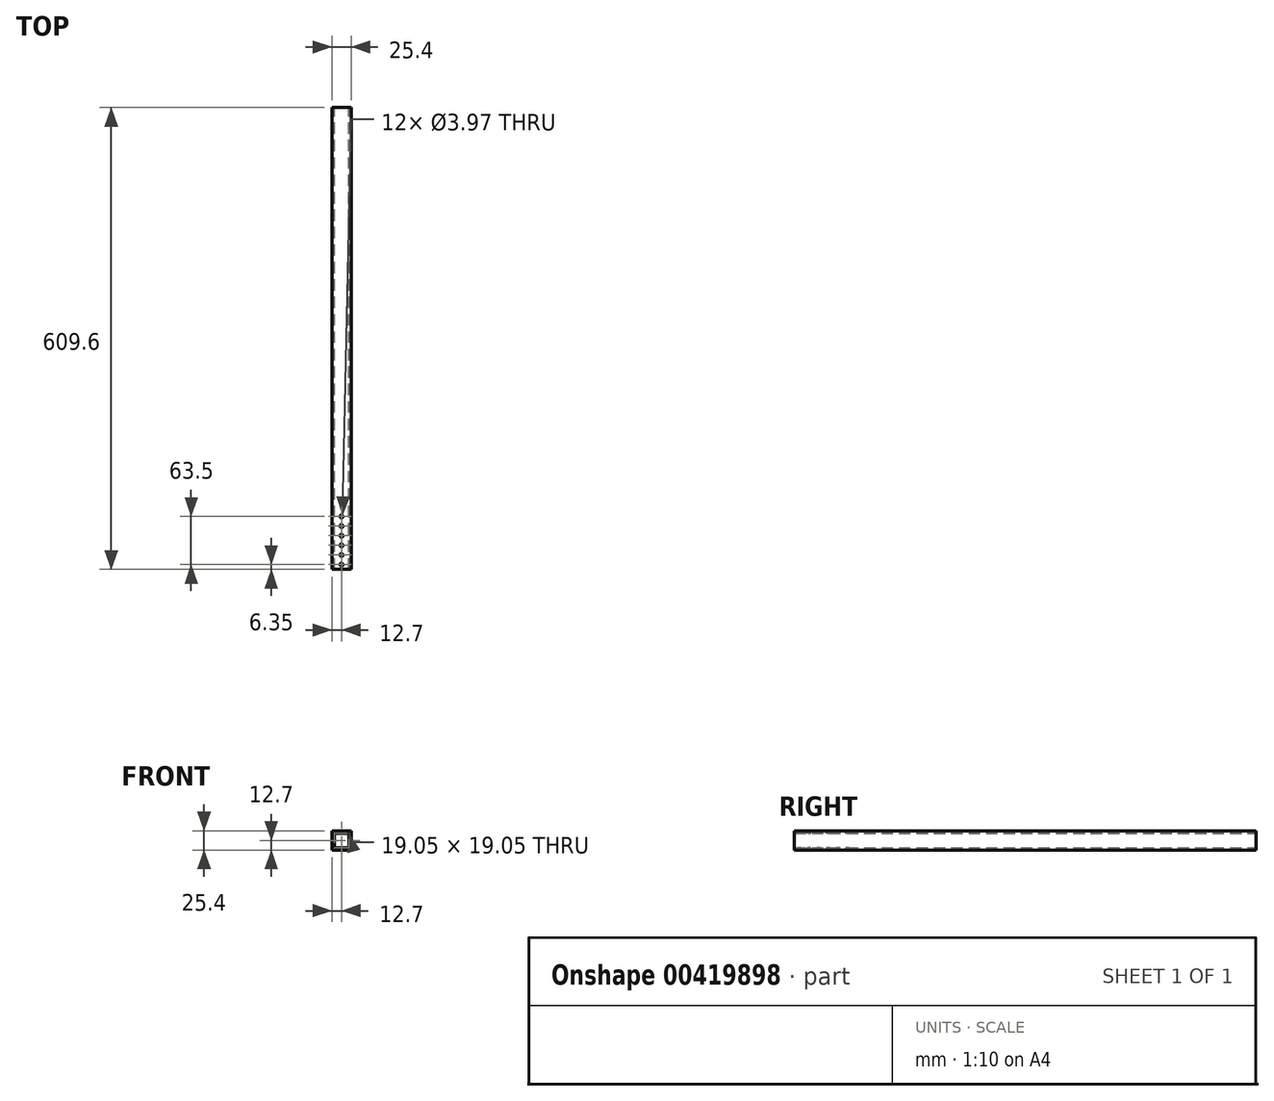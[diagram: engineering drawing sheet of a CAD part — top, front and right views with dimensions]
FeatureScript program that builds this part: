
annotation { "Feature Type Name" : "Feature", "Feature Type Description" : "" }
export const myFeature = defineFeature(function(context is Context, id is Id, definition is map)
    precondition{}
    {
        {
            var Q0;
            Q0=qCreatedBy(makeId("Front.planeOp"),FACE);
            var sketch = newSketch(context, id + "F0", { "sketchPlane" : qUnion([Q0])});
            skPoint(sketch, "E0.middle", {"position": v(0, 0) * mm});
            skLineSegment(sketch, "E1.bottom", {"start": v(12.7, 12.7) * mm, "end": v(-12.7, 12.7) * mm});
            skLineSegment(sketch, "E1.top", {"start": v(12.7, -12.7) * mm, "end": v(-12.7, -12.7) * mm});
            skLineSegment(sketch, "E1.left", {"start": v(12.7, 12.7) * mm, "end": v(12.7, -12.7) * mm});
            skLineSegment(sketch, "E1.right", {"start": v(-12.7, 12.7) * mm, "end": v(-12.7, -12.7) * mm});
            skLineSegment(sketch, "E2.bottom", {"start": v(9.52, 9.53) * mm, "end": v(-9.53, 9.53) * mm});
            skLineSegment(sketch, "E2.top", {"start": v(9.53, -9.53) * mm, "end": v(-9.52, -9.53) * mm});
            skLineSegment(sketch, "E2.left", {"start": v(9.52, 9.53) * mm, "end": v(9.53, -9.53) * mm});
            skLineSegment(sketch, "E2.right", {"start": v(-9.53, 9.53) * mm, "end": v(-9.52, -9.53) * mm});
            skSolve(sketch);
        }
        {
            var Q0;
            Q0 = qSketchRegion(id + "F0", true);
            extrude(context, id + "F1", {"entities" : qUnion([Q0]), "endBound" : BoundingType.SYMMETRIC, "depth" : 609.6 * mm});
        }
        {
            var Q0;
            Q0=makeQuery(id+"F1.opExtrude","SWEPT_FACE",FACE,{"disambiguationData":[OSD([sQuery(id+"F0.wireOp",EDGE,"E1.bottom")])]});
            var sketch = newSketch(context, id + "F2", { "sketchPlane" : qUnion([Q0])});
            skCircle(sketch, "E3", {"center": v(0, -298.45) * mm, "radius": 1.98 * mm});
            skCircle(sketch, "E4", {"center": v(0, -112.92) * mm, "radius": 1.36 * mm});
            skCircle(sketch, "E5", {"center": v(0, -107.45) * mm, "radius": 1.5 * mm});
            skCircle(sketch, "E6", {"center": v(0, -285.75) * mm, "radius": 1.98 * mm});
            skCircle(sketch, "E7.0.1.0", {"center": v(0, -273.05) * mm, "radius": 1.98 * mm});
            skCircle(sketch, "E7.0.2.0", {"center": v(0, -260.35) * mm, "radius": 1.98 * mm});
            skCircle(sketch, "E7.0.3.0", {"center": v(0, -247.65) * mm, "radius": 1.98 * mm});
            skCircle(sketch, "E7.0.4.0", {"center": v(0, -234.95) * mm, "radius": 1.98 * mm});
            skCircle(sketch, "E7.0.5.0", {"center": v(0, -222.25) * mm, "radius": 1.98 * mm});
            skCircle(sketch, "E7.0.6.0", {"center": v(0, -209.55) * mm, "radius": 1.98 * mm});
            skCircle(sketch, "E7.0.7.0", {"center": v(0, -196.85) * mm, "radius": 1.98 * mm});
            skCircle(sketch, "E7.0.8.0", {"center": v(0, -184.15) * mm, "radius": 1.98 * mm});
            skCircle(sketch, "E7.0.9.0", {"center": v(0, -171.45) * mm, "radius": 1.98 * mm});
            skCircle(sketch, "E7.0.10.0", {"center": v(0, -158.75) * mm, "radius": 1.98 * mm});
            skCircle(sketch, "E7.0.11.0", {"center": v(0, -146.05) * mm, "radius": 1.98 * mm});
            skCircle(sketch, "E7.0.12.0", {"center": v(0, -133.35) * mm, "radius": 1.98 * mm});
            skCircle(sketch, "E7.0.13.0", {"center": v(0, -120.65) * mm, "radius": 1.98 * mm});
            skCircle(sketch, "E7.0.14.0", {"center": v(0, -107.95) * mm, "radius": 1.98 * mm});
            skCircle(sketch, "E7.0.15.0", {"center": v(0, -95.25) * mm, "radius": 1.98 * mm});
            skCircle(sketch, "E7.0.16.0", {"center": v(0, -82.55) * mm, "radius": 1.98 * mm});
            skCircle(sketch, "E7.0.17.0", {"center": v(0, -69.85) * mm, "radius": 1.98 * mm});
            skCircle(sketch, "E7.0.18.0", {"center": v(0, -57.15) * mm, "radius": 1.98 * mm});
            skCircle(sketch, "E7.0.19.0", {"center": v(0, -44.45) * mm, "radius": 1.98 * mm});
            skLineSegment(sketch, "E7.direction1", {"start": v(0, -285.75) * mm, "end": v(25.4, -285.75) * mm, "construction": true});
            skLineSegment(sketch, "E7.direction2", {"start": v(0, -285.75) * mm, "end": v(0, -273.05) * mm, "construction": true});
            skSolve(sketch);
        }
        {
            var Q0;
            Q0=sQuery(id+"F2.wireOp",VERTEX,"E7.0.4.0.center");
            var Q1;
            Q1=sQuery(id+"F2.wireOp",VERTEX,"E7.0.3.0.center");
            var Q2;
            Q2=sQuery(id+"F2.wireOp",VERTEX,"E7.0.2.0.center");
            var Q3;
            Q3=sQuery(id+"F2.wireOp",VERTEX,"E7.0.1.0.center");
            var Q4;
            Q4=sQuery(id+"F2.wireOp",VERTEX,"E6.center");
            var Q5;
            Q5=sQuery(id+"F2.wireOp",VERTEX,"E3.center");
            var Q6;
            Q6=makeQuery(id+"F1.opExtrude","SWEPT_BODY",BODY,{"disambiguationData":[OSD([sQuery(id+"F0.wireOp",EDGE,"E1.bottom"),sQuery(id+"F0.wireOp",EDGE,"E1.top"),sQuery(id+"F0.wireOp",EDGE,"E1.left"),sQuery(id+"F0.wireOp",EDGE,"E1.right"),sQuery(id+"F0.wireOp",EDGE,"E2.bottom"),sQuery(id+"F0.wireOp",EDGE,"E2.top"),sQuery(id+"F0.wireOp",EDGE,"E2.left"),sQuery(id+"F0.wireOp",EDGE,"E2.right")])]});
            hole(context, id + "F3", {"style" : HoleStyle.SIMPLE, "endStyle" : HoleEndStyle.THROUGH, "holeDiameter" : 3.97 * mm, "isTappedThrough" : true, "tappedDepth" : 12.7 * mm, "tapClearance" : 3, "locations" : qUnion([Q0, Q1, Q2, Q3, Q4, Q5]), "scope" : qUnion([Q6])});
        }
    });
